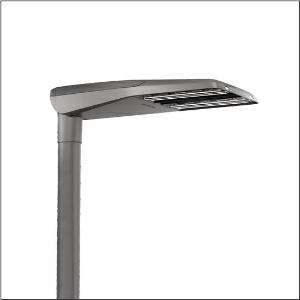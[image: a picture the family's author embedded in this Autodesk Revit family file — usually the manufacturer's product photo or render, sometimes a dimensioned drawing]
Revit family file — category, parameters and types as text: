
# Revit family: streetlight_sl_11_iq_midi___st1_2a_5xc3a51e08me_cf1e
name_source: partatom
category: Lighting Fixtures
units: mm (PartAtom-declared; Revit-internal decimal feet)

## family parameters
Cut with Voids When Loaded = No
Host = Face
Light Source = No
Part Type = Normal
Room Calculation Point = No
Round Connector Dimension = Use Diameter
Shared = No

## types (1)
- --- (1 x LED, 18110 lm, 124.7 W, 3000K)
    Apparent Load = 125 VA
    CIE Flux Codes = 32 70 96 100 100
    Color Rendering = 70
    Color Temperature = 3000K
    Default Elevation = 1800 mm
    Description = Streetlight SL 11 iQ midi, mast luminaire, primary light control with 3 zone facetted reflector, of plastic, silver coated, highly specular, primary optical cover: cover, of PMMA, transparent, light distribution: ST1.2a, light emission: direct distribution, primary light characteristic: asymmetric, installation type: post-top, side-entry, LED, High Power LED, rated luminous flux: 18.110lm, luminous efficacy: 145lm/W, light colour: 730, colour temperature: 3000K, control: optimised constant luminous flux control (CLO 2.0), Desk-Remote (wireless, voltage-free reading and setting of iQ features in the workshop via application-optimized NFC function/RFID function), Light-Fading, Smart-Wire, Night-Set, Lumen-Switch, Temp-Guard, Auto-Match, with cable H07RN-F 5x 1.5mm², mains connection: 230..240V, AC, 50/60Hz, connection cable pre-assembled, cable length: 12,5m, start of lifetime: 125W, end of service life: 132W, reduction: 57W, luminaire housing, of diecast aluminium, powder-coated, Siteco® metallic grey (DB 702S), please order mast flange separately, inclination adjustable without tools: 0°, 5°, 10°, 15° (post-top) | 0°, -5°, -10°, -15° (side-entry), sealing non-destructively replaceable, multi-level sealing system, length: 780mm, width: 376mm, height: 118mm, mast flange for spigot size: 42mm (side-entry): 5XC10008XM4, 60/48mm (side-entry/post-top): 5XC10108XM2, 76/60mm (side-entry/post-top): 5XC10108XM1, equipment: Power, protection rating (complete): IP66, insulation class (complete): insulation class II (safety insulation), certification: CE, ENEC, VDE, impact resistance: IK09, permissible operating ambient temperature for outdoor applications: -25..+50°C, standard-compliant lighting for roads and squares, Environmental Product Declaration (EPD) tested and certified by an independent institute, packaging unit: 1 piece

Light Distribution: ST1.2a
    Height = 118 mm
    Lamp = 1 x LED
    Lamp Light Flux = 18110 lm
    Lamp Power = 124.7 W
    Lamp count = 1
    Length = 780 mm
    Luminous efficacy = 145 lm/W
    Manufacturer = Siteco
    ModVariant = No
    Model = 5XC3A51E08ME
    Number of Poles = 1
    OnlyDefault = Yes
    Power Factor = 1
    Product Name = Streetlight SL 11 iQ midi | ST1.2a
    Product group = mast luminaire | pylon top
    ProductGroupID = 6100
    Protection Class = Protection class II
    Protection Degree = IP 66
    RLX_Detail_Level = 1
    RLX_Emergency_Light_Flux = 0 lm
    RLX_Emergency_Type = 0
    RLX_Emergency_Type_DB = No
    RlxData = <blob elided: 70757 chars, md5=7558efb9>
    Socket = socket
    Standby Power = 0 W
    System Light Flux = 18110 lm
    System Power = 125 W
    Type Comments = factory setting: luminous flux: 100 % | dim-lin: 254 | 557 mA
    Type Image = l_1005960.jpg
    URL = http://relux.com
    VarID = @adj_131737
    Voltage = 0 V
    Weight = 0.00 kg
    Width = 376 mm

## geometry (parser evidence)
native form markers: Blend x4, Sweep x9
no freeform markers — native parametric forms only
